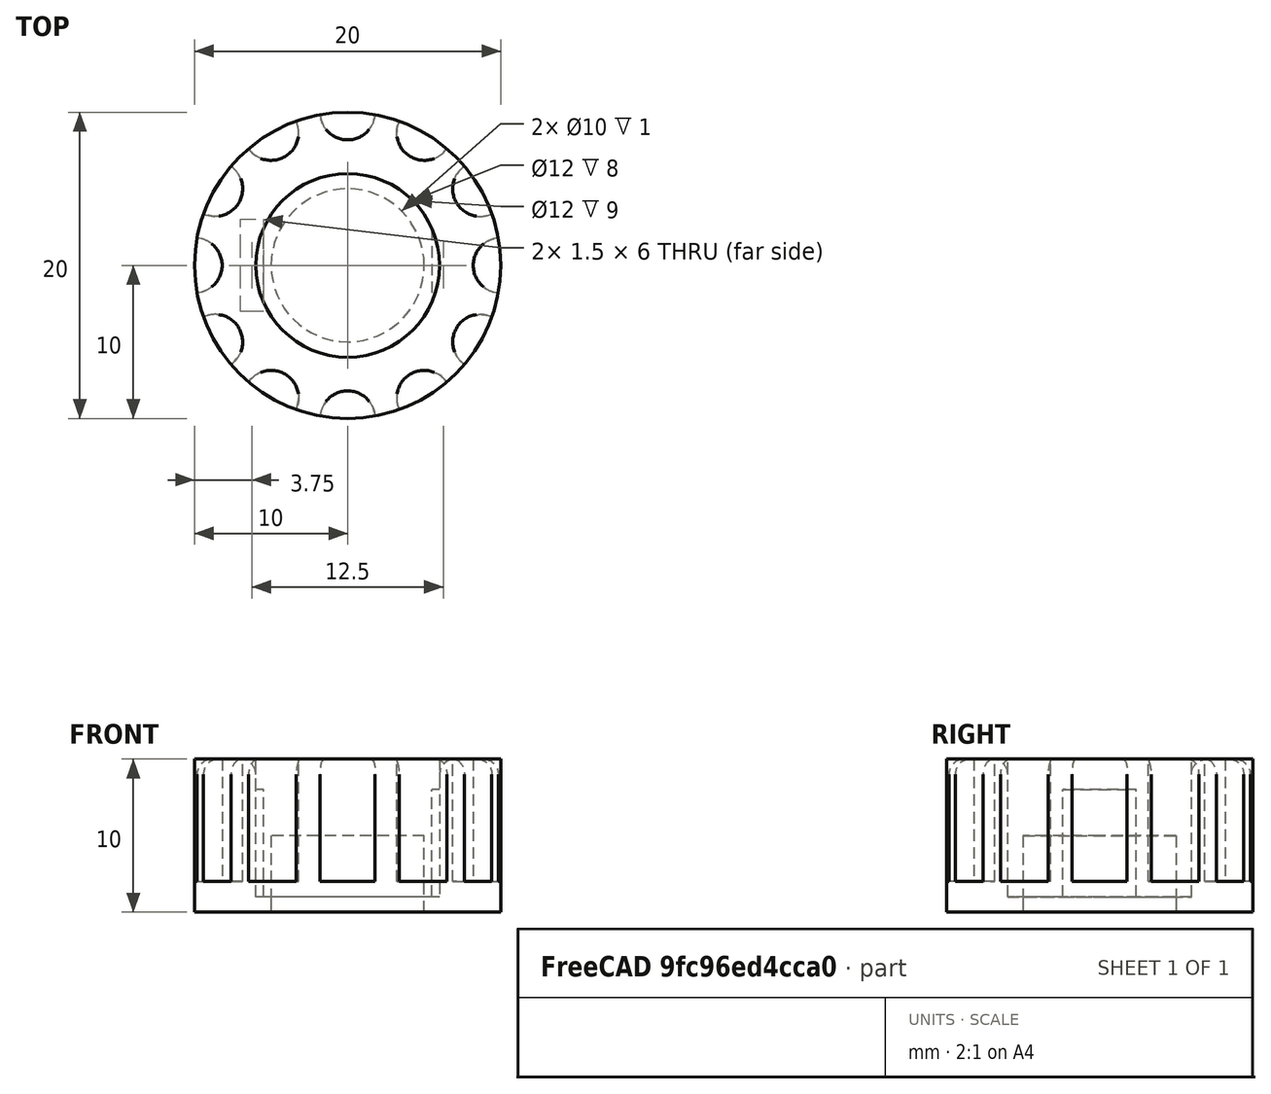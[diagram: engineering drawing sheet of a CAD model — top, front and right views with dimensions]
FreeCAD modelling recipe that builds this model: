
FCSTD DOCUMENT  (FreeCAD 0.16R)
Label: ValveNut
License: All rights reserved
LicenseURL: http://en.wikipedia.org/wiki/All_rights_reserved
objects: Sketcher::SketchObject×5, PartDesign::Pocket×3, PartDesign::Pad×2, PartDesign::Fillet×2, PartDesign::Mirrored×1, PartDesign::PolarPattern×1, Mesh::Feature×1
note: 19 computed .brp shape members not serialized (recipe doc carries the construction recipe); baked Part::Feature solids carry a one-line shape summary decoded from their .brp

FEATURE [Sketcher::SketchObject] Sketch
  sketch-geometry (1):
    g0: Circle CenterX=0 CenterY=0 CenterZ=0 NormalX=0 NormalY=0 NormalZ=1 Radius=10
  constraints (2):
    c: Coincident(g0,g-1)
    c: Radius(g0) = 10
FEATURE [PartDesign::Pad] Pad
  Length = 10
  Length2 = 100
  Sketch = -> Sketch
  Type = 0
FEATURE [Sketcher::SketchObject] Sketch001
  Placement = pos=(0,0,10) rot=(0,0,1;0rad)
  Support = -> Pad [Face3]
  sketch-geometry (1):
    g0: Circle CenterX=0 CenterY=0 CenterZ=0 NormalX=0 NormalY=0 NormalZ=1 Radius=6
  constraints (2):
    c: Coincident(g0,g-1)
    c: Radius(g0) = 6
FEATURE [PartDesign::Pocket] Pocket
  Length = 9
  Sketch = -> Sketch001
  Type = 0
FEATURE [Sketcher::SketchObject] Sketch002
  Placement = pos=(0,0,0) rot=(1,0,0;3.14159rad)
  Support = -> Pocket [Face2]
  sketch-geometry (1):
    g0: Circle CenterX=0 CenterY=0 CenterZ=0 NormalX=0 NormalY=0 NormalZ=1 Radius=5
  constraints (2):
    c: Coincident(g0,g-1)
    c: Radius(g0) = 5
FEATURE [PartDesign::Pocket] Pocket001
  Length = 5
  Sketch = -> Sketch002
  Type = 0
FEATURE [Sketcher::SketchObject] Sketch003
  Placement = pos=(0,0,0) rot=(1,0,0;3.14159rad)
  Support = -> Pocket001 [Face2]
  sketch-geometry (4):
    g0: LineSegment StartX=5.5 StartY=3 StartZ=0 EndX=7 EndY=3 EndZ=0
    g1: LineSegment StartX=7 StartY=3 StartZ=0 EndX=7 EndY=-3 EndZ=0
    g2: LineSegment StartX=7 StartY=-3 StartZ=0 EndX=5.5 EndY=-3 EndZ=0
    g3: LineSegment StartX=5.5 StartY=-3 StartZ=0 EndX=5.5 EndY=3 EndZ=0
  constraints (12):
    c: Coincident(g0,g1)
    c: Coincident(g1,g2)
    c: Coincident(g2,g3)
    c: Coincident(g3,g0)
    c: Horizontal(g0)
    c: Horizontal(g2)
    c: Vertical(g1)
    c: Vertical(g3)
    c: Symmetric(g0,g2,g-1)
    c: DistanceX(g0) = 5.5
    c: Distance(g0) = 1.5
    c: Distance(g3) = 6
FEATURE [PartDesign::Pad] Pad001
  Length = 8
  Length2 = 100
  Reversed = true
  Sketch = -> Sketch003
  Type = 0
FEATURE [PartDesign::Mirrored] Mirrored
  MirrorPlane = -> Sketch003 [V_Axis]
  Originals = -> [Pad001]
FEATURE [Sketcher::SketchObject] Sketch004
  Placement = pos=(0,0,10) rot=(0,0,1;0rad)
  Support = -> Mirrored [Face3]
  sketch-geometry (1):
    g0: Circle CenterX=-10 CenterY=0 CenterZ=0 NormalX=0 NormalY=0 NormalZ=1 Radius=1.8
  constraints (3):
    c: PointOnObject(g0,g-1)
    c: Radius(g0) = 1.8
    c: DistanceX(g0) = -10
FEATURE [PartDesign::Pocket] Pocket002
  Length = 8
  Sketch = -> Sketch004
  Type = 0
FEATURE [PartDesign::PolarPattern] PolarPattern
  Angle = 360
  Axis = -> Sketch004 [N_Axis]
  Occurrences = 12
  Originals = -> [Pocket002]
FEATURE [PartDesign::Fillet] Fillet
  Base = -> PolarPattern [Edge79]
  Radius = 1
FEATURE [PartDesign::Fillet] Fillet001
  Base = -> Fillet [Edge10,Edge13,Edge16,Edge19,Edge22,Edge25,Edge28,Edge31,Edge34,Edge37,Edge4,Edge7]
  Radius = 1
FEATURE [Mesh::Feature] Mesh  label="Fillet001 (Meshed)"
